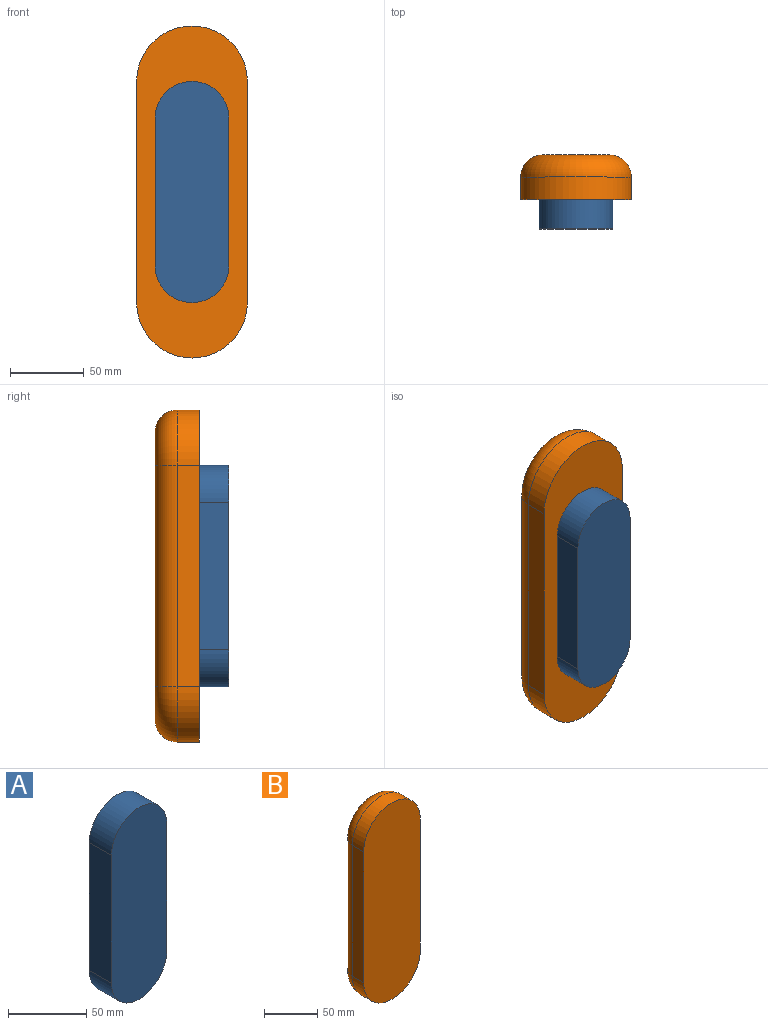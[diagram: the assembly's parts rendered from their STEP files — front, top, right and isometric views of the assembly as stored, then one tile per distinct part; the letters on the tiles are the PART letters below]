
ASSEMBLY  parts=2 mates=1
PART A: 6 faces, bbox 50x20x150 mm
  f0: plane 100x20mm, normal (-1,0,0), area 2000mm2, adj f1,f3,f4,f5
  f1: cylinder r=25mm len=50mm, axis (0,1,0), area 1570.8mm2, adj f0,f2,f4,f5
  f2: plane 100x20mm, normal (1,0,0), area 2000mm2, adj f1,f3,f4,f5
  f3: cylinder r=25mm len=50mm, axis (0,1,0), area 1570.8mm2, adj f0,f2,f4,f5
  f4: plane 150x50mm, normal (0,-1,0), area 6963.5mm2, adj f0,f1,f2,f3
  f5: plane 150x50mm, normal (0,1,0), area 6963.5mm2, adj f0,f1,f2,f3
PART B: 10 faces, bbox 81.2x30x231.2 mm
  f0: plane 150x15mm, normal (-1,0,0), area 2250mm2, adj f1,f3,f4,f6
  f1: cylinder r=37.5mm len=75mm, axis (0,1,0), area 1767.1mm2, adj f0,f2,f4,f8
  f2: plane 150x15mm, normal (1,0,0), area 2250mm2, adj f1,f3,f4,f9
  f3: cylinder r=37.5mm len=75mm, axis (0,1,0), area 1767.1mm2, adj f0,f2,f4,f7
  f4: plane 225x75mm, normal (0,-1,0), area 15667.9mm2, adj f0,f1,f2,f3
  f5: plane 195x45mm, normal (0,1,0), area 8340.4mm2, adj f6,f7,f8,f9
  f6: cylinder r=15mm len=150mm, axis (0,0,-1), area 3534.3mm2, adj f0,f5,f7,f8
  f7: torus R=22.5mm, axis (0,-1,0), area 2372.4mm2, adj f3,f5,f6,f9
  f8: torus R=22.5mm, axis (0,-1,0), area 2372.4mm2, adj f1,f5,f6,f9
  f9: cylinder r=15mm len=150mm, axis (0,0,1), area 3534.3mm2, adj f2,f5,f7,f8
PLACE A t=(-3.23,-48.3,-50.32)mm
PLACE B t=(-26.51,-18.3,-63.89)mm
MATE fastened B.f4 <-> A.f5  axis (0,-1,0) through (-17.83,-48.3,24.65)mm
